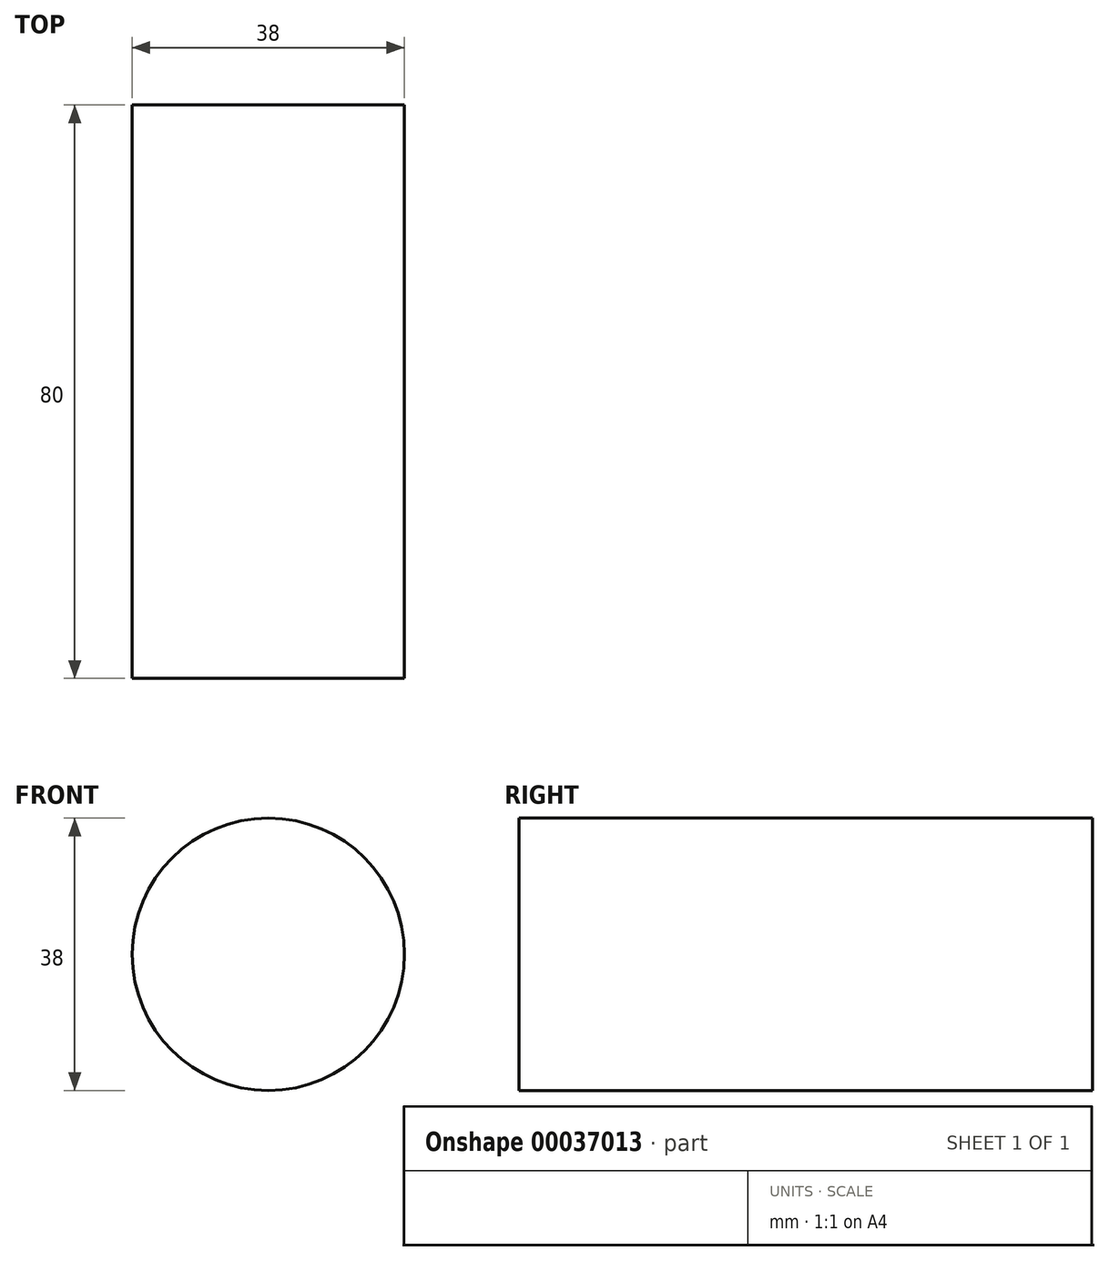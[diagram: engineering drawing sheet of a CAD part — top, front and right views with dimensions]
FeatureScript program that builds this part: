
annotation { "Feature Type Name" : "Feature", "Feature Type Description" : "" }
export const myFeature = defineFeature(function(context is Context, id is Id, definition is map)
    precondition{}
    {
        {
            var Q0;
            Q0=qCreatedBy(makeId("Front.planeOp"),FACE);
            var sketch = newSketch(context, id + "F0", { "sketchPlane" : qUnion([Q0])});
            skCircle(sketch, "E0", {"center": v(0, 0) * mm, "radius": 19 * mm});
            skSolve(sketch);
        }
        {
            var Q0;
            Q0 = qSketchRegion(id + "F0", true);
            extrude(context, id + "F1", {"entities" : qUnion([Q0]), "depth" : 80 * mm});
        }
    });
